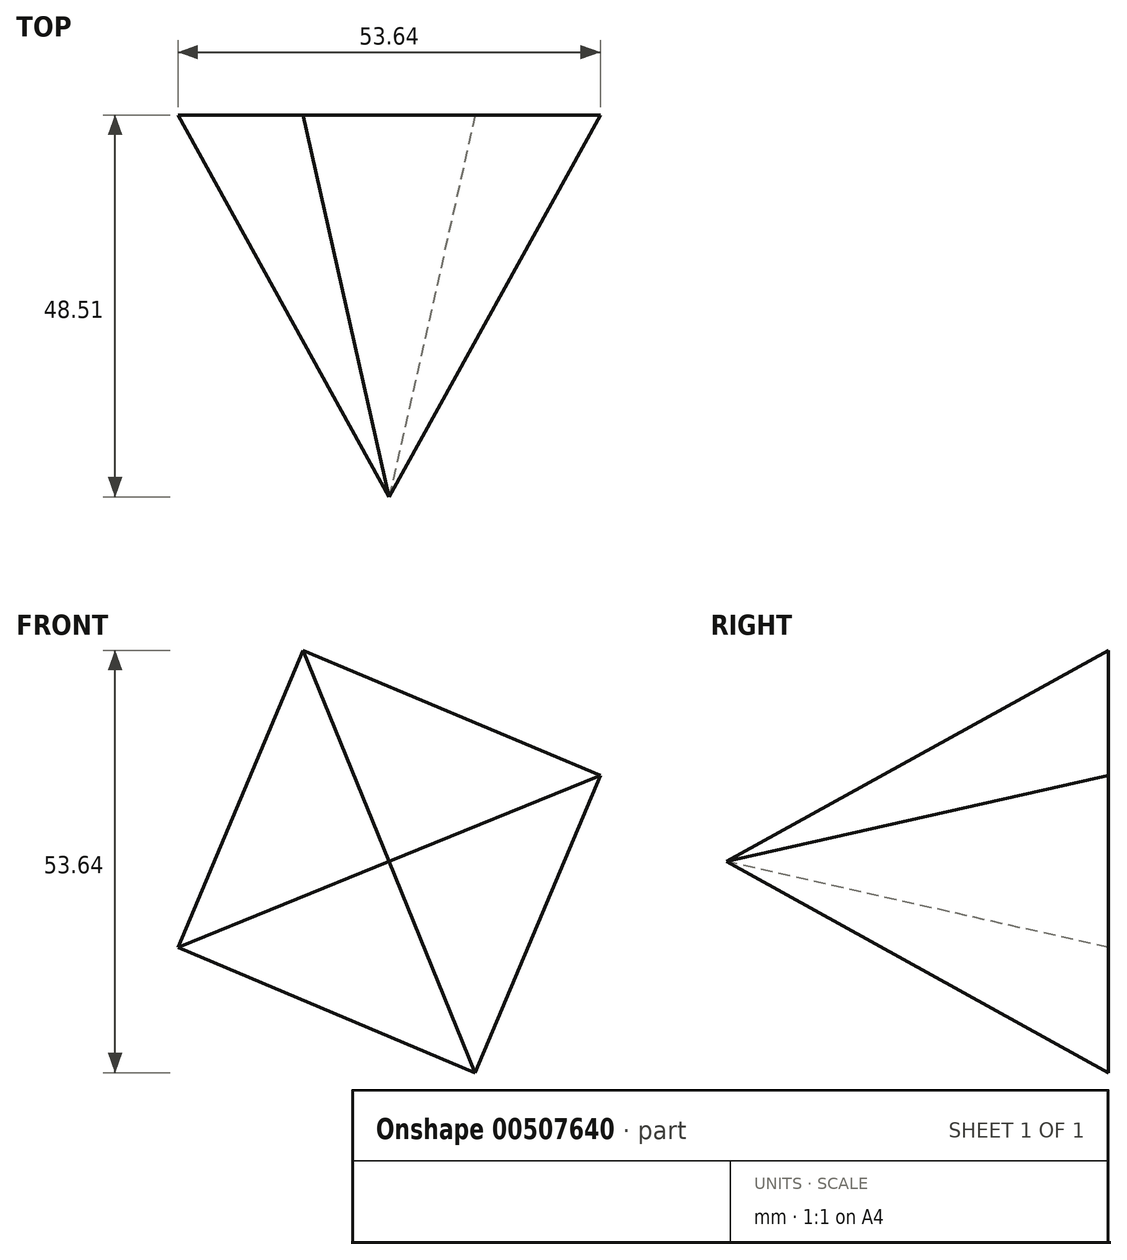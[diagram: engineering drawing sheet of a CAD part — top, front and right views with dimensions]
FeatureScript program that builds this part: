
annotation { "Feature Type Name" : "Feature", "Feature Type Description" : "" }
export const myFeature = defineFeature(function(context is Context, id is Id, definition is map)
    precondition{}
    {
        {
            var Q0;
            Q0=qCreatedBy(makeId("Front.planeOp"),FACE);
            var sketch = newSketch(context, id + "F0", { "sketchPlane" : qUnion([Q0])});
            skCircle(sketch, "E0.cCircle", {"center": v(0, 0) * mm, "radius": 28.96 * mm, "construction": true});
            skLineSegment(sketch, "E0.0", {"start": v(26.82, 10.93) * mm, "end": v(10.93, -26.82) * mm});
            skLineSegment(sketch, "E0.1", {"start": v(10.93, -26.82) * mm, "end": v(-26.82, -10.93) * mm});
            skLineSegment(sketch, "E0.2", {"start": v(-26.82, -10.93) * mm, "end": v(-10.93, 26.82) * mm});
            skLineSegment(sketch, "E0.3", {"start": v(-10.93, 26.82) * mm, "end": v(26.82, 10.93) * mm});
            skSolve(sketch);
        }
        {
            var Q0;
            Q0=qCreatedBy(makeId("Front.planeOp"),FACE);
            cPlane(context, id + "F1", {"entities" : qUnion([Q0]), "cplaneType" : CPlaneType.OFFSET, "offset" : 48.5 * mm, "width" : 152.4 * mm, "height" : 152.4 * mm});
        }
        {
            var Q0;
            Q0=qCreatedBy(id+"F1.planeOp",FACE);
            var sketch = newSketch(context, id + "F2", { "sketchPlane" : qUnion([Q0])});
            skCircle(sketch, "E1", {"center": v(0, 0) * mm, "radius": 1.95 * mm});
            skSolve(sketch);
        }
        {
            var Q0;
            Q0=makeQuery(id+"F0.imprint","IMPRINT",FACE,{"disambiguationData":[TD([[makeQuery(id+"F0.imprint","IMPRINT",EDGE,{"derivedFrom":sQuery(id+"F0.wireOp",EDGE,"E0.0")}),-1.0]])]});
            var Q1;
            Q1=sQuery(id+"F2.wireOp",VERTEX,"E1.center");
            loft(context, id + "F3", {"sheetProfilesArray" : [{ "sheetProfileEntities" : qUnion([Q0]) }, { "sheetProfileEntities" : qUnion([Q1]) }]});
        }
    });
